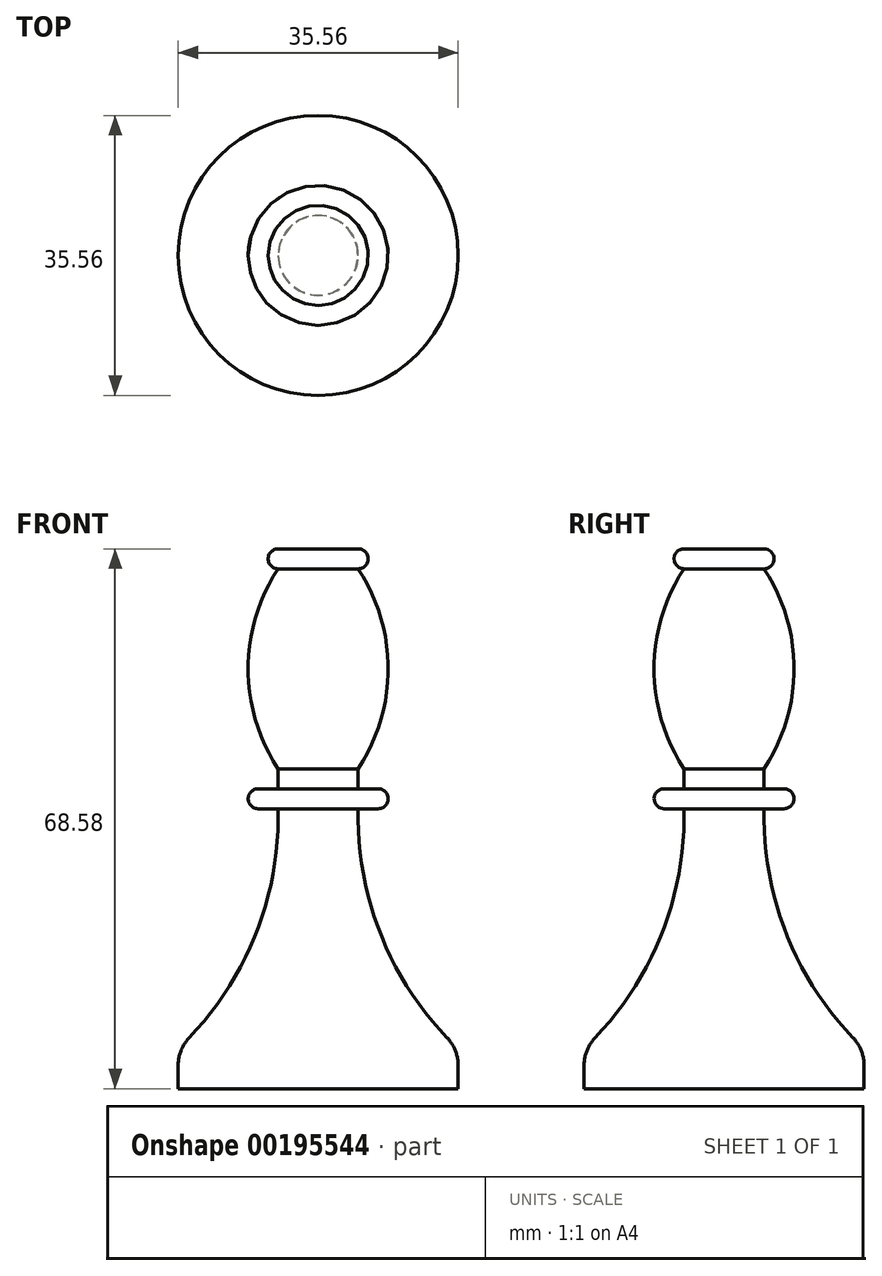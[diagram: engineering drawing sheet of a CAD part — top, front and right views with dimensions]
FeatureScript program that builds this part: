
annotation { "Feature Type Name" : "Feature", "Feature Type Description" : "" }
export const myFeature = defineFeature(function(context is Context, id is Id, definition is map)
    precondition{}
    {
        {
            var Q0;
            Q0=qCreatedBy(makeId("Front.planeOp"),FACE);
            var sketch = newSketch(context, id + "F0", { "sketchPlane" : qUnion([Q0])});
            skLineSegment(sketch, "E0", {"start": v(0, 0) * mm, "end": v(0, 68.58) * mm});
            skLineSegment(sketch, "E1", {"start": v(0, 0) * mm, "end": v(17.78, 0) * mm});
            skLineSegment(sketch, "E2", {"start": v(17.78, 0) * mm, "end": v(17.78, 5.08) * mm});
            skArc(sketch, "E3", {"start": v(5.08, 35.56) * mm, "mid": v(8.2, 18.97) * mm, "end": v(17.78, 5.08) * mm});
            skLineSegment(sketch, "E4", {"start": v(0, 68.58) * mm, "end": v(5.08, 68.58) * mm});
            skArc(sketch, "E5", {"start": v(5.08, 66.04) * mm, "mid": v(6.35, 67.31) * mm, "end": v(5.08, 68.58) * mm});
            skLineSegment(sketch, "E6", {"start": v(5.08, 35.56) * mm, "end": v(7.62, 35.56) * mm});
            skLineSegment(sketch, "E7", {"start": v(7.62, 38.1) * mm, "end": v(5.08, 38.1) * mm});
            skLineSegment(sketch, "E8", {"start": v(5.08, 38.1) * mm, "end": v(5.08, 40.64) * mm});
            skArc(sketch, "E9", {"start": v(5.08, 40.64) * mm, "mid": v(8.89, 53.34) * mm, "end": v(5.08, 66.04) * mm});
            skArc(sketch, "E10", {"start": v(7.62, 35.56) * mm, "mid": v(8.9, 36.83) * mm, "end": v(7.62, 38.1) * mm});
            skPoint(sketch, "E11.end.orphan", {"position": v(0, 60.96) * mm});
            skPoint(sketch, "E12.orphan", {"position": v(0, 38.1) * mm});
            skPoint(sketch, "E13.end.orphan", {"position": v(0, 35.56) * mm});
            skSolve(sketch);
        }
        {
            var Q0;
            Q0=makeQuery(id+"F0.imprint","IMPRINT",FACE,{"disambiguationData":[TD([[makeQuery(id+"F0.imprint","IMPRINT",EDGE,{"derivedFrom":sQuery(id+"F0.wireOp",EDGE,"E0")}),-1.0]])]});
            var Q1;
            Q1=sQuery(id+"F0.wireOp",EDGE,"E0");
            revolve(context, id + "F1", {"entities" : qUnion([Q0]), "axis" : qUnion([Q1]), "revolveType" : RevolveType.FULL});
        }
        {
            var Q0;
            Q0=makeQuery(id+"F1.opRevolve","SWEPT_EDGE",EDGE,{"disambiguationData":[OSD([sQuery(id+"F0.wireOp",EDGE,"E2"),sQuery(id+"F0.wireOp",EDGE,"E3")])]});
            fillet(context, id + "F2", {"entities" : qUnion([Q0]), "radius" : 5.08 * mm, "tangentPropagation" : true, "allowEdgeOverflow" : false});
        }
    });
